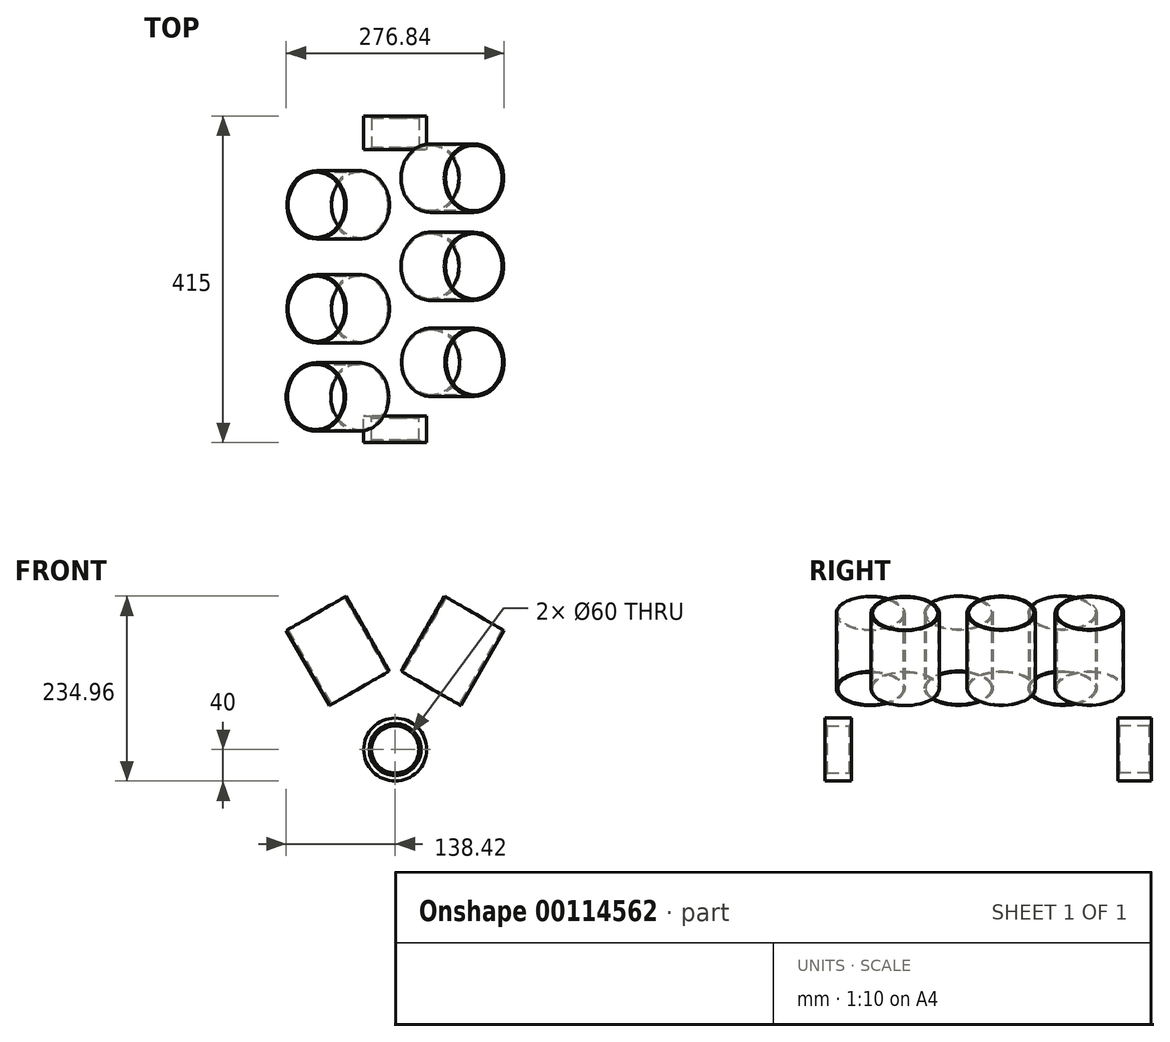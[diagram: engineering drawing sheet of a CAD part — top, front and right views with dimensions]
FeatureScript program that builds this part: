
annotation { "Feature Type Name" : "Feature", "Feature Type Description" : "" }
export const myFeature = defineFeature(function(context is Context, id is Id, definition is map)
    precondition{}
    {
        {
            var Q0;
            Q0=qCreatedBy(makeId("Front.planeOp"),FACE);
            var sketch = newSketch(context, id + "F0", { "sketchPlane" : qUnion([Q0])});
            skCircle(sketch, "E0", {"center": v(0, 0) * mm, "radius": 30 * mm});
            skCircle(sketch, "E1", {"center": v(0, 0) * mm, "radius": 40 * mm});
            skSolve(sketch);
        }
        {
            var Q0;
            Q0=qSketchRegion(id+"F0",true);
            extrude(context, id + "F1", {"entities" : qUnion([Q0]), "depth" : 34 * mm});
        }
        {
            var Q0;
            Q0=qCreatedBy(makeId("Front.planeOp"),FACE);
            cPlane(context, id + "F2", {"entities" : qUnion([Q0]), "cplaneType" : CPlaneType.OFFSET, "offset" : 338 * mm, "oppositeDirection" : true, "width" : 150 * mm, "height" : 150 * mm});
        }
        {
            var Q0;
            Q0=qCreatedBy(id+"F2.planeOp",FACE);
            var sketch = newSketch(context, id + "F3", { "sketchPlane" : qUnion([Q0])});
            skCircle(sketch, "E2", {"center": v(0, 0) * mm, "radius": 30 * mm});
            skCircle(sketch, "E3", {"center": v(0, 0) * mm, "radius": 40 * mm});
            skSolve(sketch);
        }
        {
            var Q0;
            Q0=qSketchRegion(id+"F3",true);
            extrude(context, id + "F4", {"entities" : qUnion([Q0]), "oppositeDirection" : true, "depth" : 43 * mm});
        }
        {
            var Q0;
            Q0=makeQuery(id+"F1.opExtrude","CAP_EDGE",EDGE,{"disambiguationData":[OSD([sQuery(id+"F0.wireOp",EDGE,"E0")])],"isStart":false});
            var Q1;
            Q1=makeQuery(id+"F1.opExtrude","CAP_EDGE",EDGE,{"disambiguationData":[OSD([sQuery(id+"F0.wireOp",EDGE,"E0")])],"isStart":true});
            var Q2;
            Q2=makeQuery(id+"F4.opExtrude","CAP_EDGE",EDGE,{"disambiguationData":[OSD([sQuery(id+"F3.wireOp",EDGE,"E2")])],"isStart":true});
            var Q3;
            Q3=makeQuery(id+"F4.opExtrude","CAP_EDGE",EDGE,{"disambiguationData":[OSD([sQuery(id+"F3.wireOp",EDGE,"E2")])],"isStart":false});
            chamfer(context, id + "F5", {"entities" : qUnion([Q0, Q1, Q2, Q3]), "width" : 3 * mm, "tangentPropagation" : true});
        }
        {
            var Q0;
            Q0=qCreatedBy(makeId("Right.planeOp"),FACE);
            var Q1;
            Q1=makeQuery(id+"F1.opExtrude","SWEPT_FACE",FACE,{"disambiguationData":[OSD([sQuery(id+"F0.wireOp",EDGE,"E1")])]});
            cPlane(context, id + "F6", {"entities" : qUnion([Q0, Q1]), "cplaneType" : CPlaneType.LINE_ANGLE, "offset" : 25 * mm, "angle" : 60 * degree, "width" : 150 * mm, "height" : 150 * mm});
        }
        {
            var Q0;
            Q0=qCreatedBy(id+"F6.planeOp",FACE);
            var sketch = newSketch(context, id + "F7", { "sketchPlane" : qUnion([Q0])});
            skLineSegment(sketch, "E4", {"start": v(43.03, 14) * mm, "end": v(-44.75, 14) * mm, "construction": true});
            skLineSegment(sketch, "E5", {"start": v(41.93, 136) * mm, "end": v(-45.38, 136) * mm, "construction": true});
            skLineSegment(sketch, "E6", {"start": v(-45.38, 258) * mm, "end": v(41.93, 258) * mm, "construction": true});
            skLineSegment(sketch, "E7", {"start": v(0, 0) * mm, "end": v(0, 322.57) * mm, "construction": true});
            skCircle(sketch, "E8", {"center": v(-0.86, 14) * mm, "radius": 41.47 * mm});
            skCircle(sketch, "E9", {"center": v(0, 136) * mm, "radius": 41.47 * mm});
            skCircle(sketch, "E10", {"center": v(0, 258) * mm, "radius": 41.47 * mm});
            skCircle(sketch, "E11", {"center": v(-0.86, 14) * mm, "radius": 43.5 * mm});
            skCircle(sketch, "E12", {"center": v(0, 136) * mm, "radius": 43.5 * mm});
            skCircle(sketch, "E13", {"center": v(0, 258) * mm, "radius": 43.5 * mm});
            skSolve(sketch);
        }
        {
            var Q0;
            Q0=qSketchRegion(id+"F7",true);
            extrude(context, id + "F8", {"entities" : qUnion([Q0]), "depth" : 200 * mm, "hasSecondDirection" : true, "secondDirectionOppositeDirection" : false, "secondDirectionDepth" : 90 * mm});
        }
        {
            var Q0;
            Q0=makeQuery(id+"F8.opExtrude","SWEPT_BODY",BODY,{"disambiguationData":[OSD([sQuery(id+"F7.wireOp",EDGE,"E10"),sQuery(id+"F7.wireOp",EDGE,"E13")])]});
            var Q1;
            Q1=makeQuery(id+"F8.opExtrude","SWEPT_BODY",BODY,{"disambiguationData":[OSD([sQuery(id+"F7.wireOp",EDGE,"E9"),sQuery(id+"F7.wireOp",EDGE,"E12")])]});
            var Q2;
            Q2=makeQuery(id+"F8.opExtrude","SWEPT_BODY",BODY,{"disambiguationData":[OSD([sQuery(id+"F7.wireOp",EDGE,"E8"),sQuery(id+"F7.wireOp",EDGE,"E11")])]});
            var Q3;
            Q3=qCreatedBy(makeId("Right.planeOp"),FACE);
            mirror(context, id + "F9", {"entities" : qUnion([Q0, Q1, Q2]), "mirrorPlane" : qUnion([Q3])});
        }
        {
            var Q0;
            Q0=makeQuery(id+"F9.opPattern","COPY",BODY,{"derivedFrom":makeQuery(id+"F8.opExtrude","SWEPT_BODY",BODY,{"disambiguationData":[OSD([sQuery(id+"F7.wireOp",EDGE,"E8"),sQuery(id+"F7.wireOp",EDGE,"E11")])]}),"instanceName":"1"});
            var Q1;
            Q1=makeQuery(id+"F9.opPattern","COPY",BODY,{"derivedFrom":makeQuery(id+"F8.opExtrude","SWEPT_BODY",BODY,{"disambiguationData":[OSD([sQuery(id+"F7.wireOp",EDGE,"E9"),sQuery(id+"F7.wireOp",EDGE,"E12")])]}),"instanceName":"1"});
            var Q2;
            Q2=makeQuery(id+"F9.opPattern","COPY",BODY,{"derivedFrom":makeQuery(id+"F8.opExtrude","SWEPT_BODY",BODY,{"disambiguationData":[OSD([sQuery(id+"F7.wireOp",EDGE,"E10"),sQuery(id+"F7.wireOp",EDGE,"E13")])]}),"instanceName":"1"});
            var Q3;
            Q3=sQuery(id+"F7.wireOp",EDGE,"E7");
            var Q4;
            Q4=sQuery(id+"F7.wireOp",EDGE,"E7");
            transform(context, id + "F10", {"entities" : qUnion([Q0, Q1, Q2]), "transformType" : TransformType.TRANSLATION_DISTANCE, "transformDirection" : qUnion([Q4]), "distance" : 44 * mm, "makeCopy" : false});
        }
        {
            var Q0;
            Q0=makeQuery(id+"F8.opExtrude","SWEPT_BODY",BODY,{"disambiguationData":[OSD([sQuery(id+"F7.wireOp",EDGE,"E8"),sQuery(id+"F7.wireOp",EDGE,"E11")])]});
            var Q1;
            Q1=makeQuery(id+"F9.opPattern","COPY",BODY,{"derivedFrom":makeQuery(id+"F8.opExtrude","SWEPT_BODY",BODY,{"disambiguationData":[OSD([sQuery(id+"F7.wireOp",EDGE,"E8"),sQuery(id+"F7.wireOp",EDGE,"E11")])]}),"instanceName":"1"});
            var Q2;
            Q2=makeQuery(id+"F9.opPattern","COPY",BODY,{"derivedFrom":makeQuery(id+"F8.opExtrude","SWEPT_BODY",BODY,{"disambiguationData":[OSD([sQuery(id+"F7.wireOp",EDGE,"E9"),sQuery(id+"F7.wireOp",EDGE,"E12")])]}),"instanceName":"1"});
            var Q3;
            Q3=makeQuery(id+"F8.opExtrude","SWEPT_BODY",BODY,{"disambiguationData":[OSD([sQuery(id+"F7.wireOp",EDGE,"E10"),sQuery(id+"F7.wireOp",EDGE,"E13")])]});
            var Q4;
            Q4=sQuery(id+"F7.wireOp",EDGE,"E7");
            transform(context, id + "F11", {"entities" : qUnion([Q0, Q1, Q2, Q3]), "transformType" : TransformType.TRANSLATION_DISTANCE, "transformDirection" : qUnion([Q4]), "distance" : 10 * mm, "makeCopy" : false});
        }
    });
